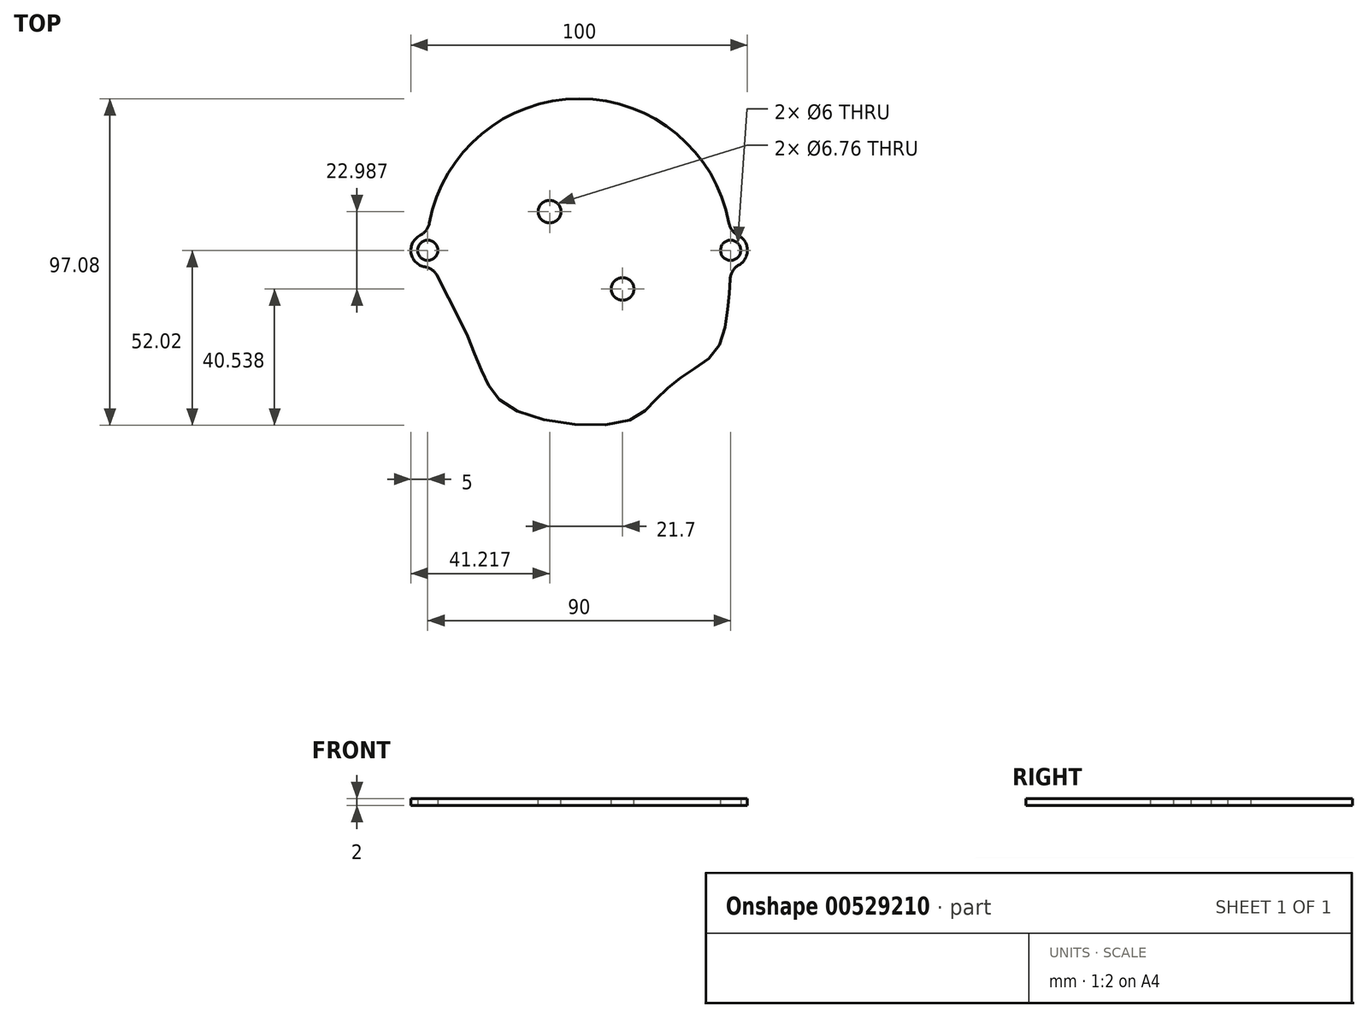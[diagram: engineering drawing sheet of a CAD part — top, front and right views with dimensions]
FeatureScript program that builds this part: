
annotation { "Feature Type Name" : "Feature", "Feature Type Description" : "" }
export const myFeature = defineFeature(function(context is Context, id is Id, definition is map)
    precondition{}
    {
        {
            var Q0;
            Q0=qCreatedBy(makeId("Top.planeOp"),FACE);
            var sketch = newSketch(context, id + "F0", { "sketchPlane" : qUnion([Q0])});
            skLineSegment(sketch, "E0", {"start": v(42.65, 0) * mm, "end": v(-47.35, 0) * mm, "construction": true});
            skLineSegment(sketch, "E1", {"start": v(0, 0) * mm, "end": v(0, 45) * mm, "construction": true});
            skLineSegment(sketch, "E2", {"start": v(0, 0) * mm, "end": v(0, -52) * mm, "construction": true});
            skCircle(sketch, "E3", {"center": v(-47.35, 0) * mm, "radius": 5 * mm});
            skCircle(sketch, "E4", {"center": v(42.65, 0) * mm, "radius": 5 * mm});
            skArc(sketch, "E5", {"start": v(42.65, 5) * mm, "mid": v(-2.35, 45.06) * mm, "end": v(-47.35, 5) * mm});
            skFitSpline(sketch, "E6", {"points": [v(42.65, -5) * mm, v(41.99, -15.63) * mm, v(38.96, -28.76) * mm, v(29.89, -36.53) * mm, v(21.29, -43.44) * mm, v(11.74, -50.8) * mm, v(-21.42, -47.53) * mm, v(-30.68, -37.23) * mm, v(-35.92, -24.72) * mm, v(-45.9, -4.79) * mm], "startDerivative": vector(-3.9, -154.94) * mm, "endDerivative": vector(-85.77, 173.48) * mm});
            skSolve(sketch);
        }
        {
            var Q0;
            {var subQ0=sQuery(id+"F0.wireOp",EDGE,"E5");Q0=makeQuery(id+"F0.imprint","IMPRINT",FACE,{"disambiguationData":[TD([[makeQuery(id+"F0.imprint","IMPRINT",EDGE,{"derivedFrom":subQ0}),1.0]])]});}
            var Q1;
            {var subQ0=sQuery(id+"F0.wireOp",EDGE,"E3");var subQ1=makeQuery(id+"F0.imprint","INTERSECT",VERTEX,{"derivedFrom":[subQ0,sQuery(id+"F0.wireOp",EDGE,"E5")]});Q1=makeQuery(id+"F0.imprint","IMPRINT",FACE,{"disambiguationData":[TD([[makeQuery(id+"F0.imprint","IMPRINT",EDGE,{"disambiguationData":[TD([[subQ1,-1.0]])],"derivedFrom":subQ0}),1.0]])]});}
            var Q2;
            {var subQ0=sQuery(id+"F0.wireOp",EDGE,"E4");var subQ1=makeQuery(id+"F0.imprint","INTERSECT",VERTEX,{"derivedFrom":[subQ0,sQuery(id+"F0.wireOp",EDGE,"E5")]});Q2=makeQuery(id+"F0.imprint","IMPRINT",FACE,{"disambiguationData":[TD([[makeQuery(id+"F0.imprint","IMPRINT",EDGE,{"disambiguationData":[TD([[subQ1,-1.0]])],"derivedFrom":subQ0}),1.0]])]});}
            extrude(context, id + "F1", {"entities" : qUnion([Q0, Q1, Q2]), "depth" : 2 * mm, "offsetDistance" : 25 * mm});
        }
        {
            var Q0;
            Q0=sQuery(id+"F0.wireOp",VERTEX,"E3.center");
            var Q1;
            Q1=sQuery(id+"F0.wireOp",VERTEX,"E4.center");
            var Q2;
            Q2=makeQuery(id+"F1.opExtrude","SWEPT_BODY",BODY,{"disambiguationData":[OSD([sQuery(id+"F0.wireOp",EDGE,"E3"),sQuery(id+"F0.wireOp",EDGE,"E4"),sQuery(id+"F0.wireOp",EDGE,"E5"),sQuery(id+"F0.wireOp",EDGE,"E6")])]});
            hole(context, id + "F2", {"style" : HoleStyle.SIMPLE, "endStyle" : HoleEndStyle.BLIND, "oppositeDirection" : true, "holeDiameter" : 6 * mm, "holeDepth" : 15 * mm, "isTappedThrough" : true, "tappedDepth" : 12 * mm, "tapClearance" : 3, "startFromSketch" : true, "locations" : qUnion([Q0, Q1]), "scope" : qUnion([Q2])});
        }
        {
            var Q0;
            Q0=makeQuery(id+"F1.opExtrude","SWEPT_EDGE",EDGE,{"disambiguationData":[OSD([sQuery(id+"F0.wireOp",EDGE,"E3"),sQuery(id+"F0.wireOp",EDGE,"E5")])]});
            var Q1;
            Q1=makeQuery(id+"F1.opExtrude","SWEPT_EDGE",EDGE,{"disambiguationData":[OSD([sQuery(id+"F0.wireOp",EDGE,"E3"),sQuery(id+"F0.wireOp",EDGE,"E6")])]});
            var Q2;
            Q2=makeQuery(id+"F1.opExtrude","SWEPT_EDGE",EDGE,{"disambiguationData":[OSD([sQuery(id+"F0.wireOp",EDGE,"E4"),sQuery(id+"F0.wireOp",EDGE,"E5")])]});
            var Q3;
            Q3=makeQuery(id+"F1.opExtrude","SWEPT_EDGE",EDGE,{"disambiguationData":[OSD([sQuery(id+"F0.wireOp",EDGE,"E4"),sQuery(id+"F0.wireOp",EDGE,"E6")])]});
            fillet(context, id + "F3", {"entities" : qUnion([Q0, Q1, Q2, Q3]), "radius" : 5 * mm, "tangentPropagation" : true, "allowEdgeOverflow" : false});
        }
        {
            var Q0;
            Q0=makeQuery(id+"F1.opExtrude","CAP_FACE",FACE,{"disambiguationData":[OSD([sQuery(id+"F0.wireOp",EDGE,"E3"),sQuery(id+"F0.wireOp",EDGE,"E4"),sQuery(id+"F0.wireOp",EDGE,"E5"),sQuery(id+"F0.wireOp",EDGE,"E6")])],"isStart":false});
            var sketch = newSketch(context, id + "F4", { "sketchPlane" : qUnion([Q0])});
            skArc(sketch, "E7", {"start": v(33.9, -33.89) * mm, "mid": v(7.74, -2.5) * mm, "end": v(29.17, 32.3) * mm, "construction": true});
            skArc(sketch, "E8", {"start": v(-31.42, 34.5) * mm, "mid": v(-9.35, -0.2) * mm, "end": v(-31.79, -34.67) * mm, "construction": true});
            skArc(sketch, "E9", {"start": v(7.94, 23.3) * mm, "mid": v(12.65, 0.59) * mm, "end": v(8.39, -22.2) * mm, "construction": true});
            skArc(sketch, "E10", {"start": v(-7.57, 22.43) * mm, "mid": v(-12.35, -0.63) * mm, "end": v(-7.04, -23.58) * mm, "construction": true});
            skPoint(sketch, "E11", {"position": v(-11.13, 11.5) * mm});
            skPoint(sketch, "E12", {"position": v(10.57, -11.48) * mm});
            skSolve(sketch);
        }
        {
            var Q0;
            Q0=sQuery(id+"F4.wireOp",VERTEX,"E11");
            var Q1;
            Q1=sQuery(id+"F4.wireOp",VERTEX,"9403577d-04ea-496b-830e-e229223042da");
            var Q2;
            Q2=sQuery(id+"F4.wireOp",VERTEX,"E12");
            var Q3;
            Q3=makeQuery(id+"F1.opExtrude","SWEPT_BODY",BODY,{"disambiguationData":[OSD([sQuery(id+"F0.wireOp",EDGE,"E3"),sQuery(id+"F0.wireOp",EDGE,"E4"),sQuery(id+"F0.wireOp",EDGE,"E5"),sQuery(id+"F0.wireOp",EDGE,"E6")])]});
            hole(context, id + "F5", {"style" : HoleStyle.SIMPLE, "endStyle" : HoleEndStyle.BLIND, "standardTappedOrClearance" : lookupTablePath({ "standard" : "ANSI", "fit" : "Normal (ASME)", "size" : "1/4", "type" : "Clearance" }), "standardBlindInLast" : lookupTablePath({ "fit" : "Free", "standard" : "ANSI", "size" : "1/4", "type" : "Clearance" }), "holeDiameter" : 6.76 * mm, "holeDepth" : 15 * mm, "isTappedThrough" : true, "tappedDepth" : 12 * mm, "tapClearance" : 3, "startFromSketch" : true, "locations" : qUnion([Q0, Q1, Q2]), "scope" : qUnion([Q3])});
        }
    });
